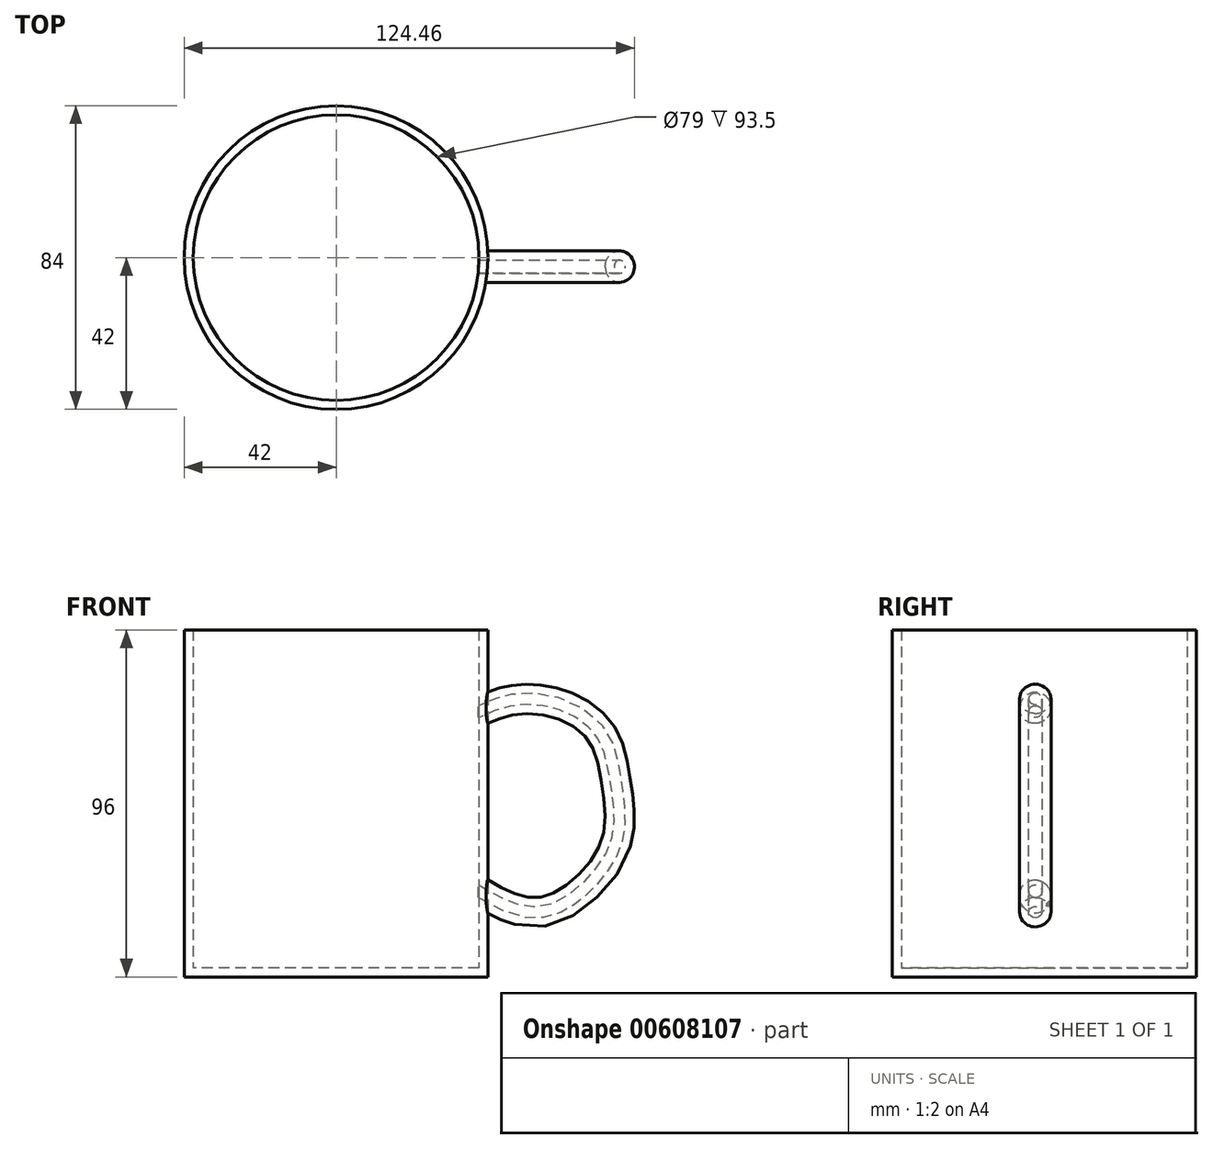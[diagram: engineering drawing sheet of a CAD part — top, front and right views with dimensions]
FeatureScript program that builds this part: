
annotation { "Feature Type Name" : "Feature", "Feature Type Description" : "" }
export const myFeature = defineFeature(function(context is Context, id is Id, definition is map)
    precondition{}
    {
        {
            var Q0;
            Q0=qCreatedBy(makeId("Top.planeOp"),FACE);
            var sketch = newSketch(context, id + "F0", { "sketchPlane" : qUnion([Q0])});
            skCircle(sketch, "E0", {"center": v(0, 0) * mm, "radius": 42 * mm});
            skSolve(sketch);
        }
        {
            var Q0;
            Q0 = qSketchRegion(id + "F0", true);
            extrude(context, id + "F1", {"entities" : qUnion([Q0]), "depth" : 96 * mm, "offsetDistance" : 25 * mm});
        }
        {
            var Q0;
            Q0=qCreatedBy(makeId("Front.planeOp"),FACE);
            var sketch = newSketch(context, id + "F2", { "sketchPlane" : qUnion([Q0])});
            skFitSpline(sketch, "E1", {"points": [v(40.8, 71.96) * mm, v(48.66, 74.63) * mm, v(60.67, 73.85) * mm, v(71.49, 66.59) * mm, v(75.33, 54.8) * mm, v(76.11, 39.69) * mm, v(69.57, 27.89) * mm, v(58.72, 20.43) * mm, v(49.27, 20.86) * mm, v(39.83, 25.62) * mm], "startDerivative": vector(79.14, 34.52) * mm, "endDerivative": vector(-88.75, 52.54) * mm});
            skSolve(sketch);
        }
        {
            var Q0;
            Q0=qCreatedBy(makeId("Right.planeOp"),FACE);
            cPlane(context, id + "F3", {"entities" : qUnion([Q0]), "cplaneType" : CPlaneType.OFFSET, "offset" : 42 * mm, "width" : 150 * mm, "height" : 150 * mm});
        }
        {
            var Q0;
            Q0=qCreatedBy(id+"F3.planeOp",FACE);
            var sketch = newSketch(context, id + "F4", { "sketchPlane" : qUnion([Q0])});
            skCircle(sketch, "E2", {"center": v(-2.5, 74.52) * mm, "radius": 4.35 * mm});
            skSolve(sketch);
        }
        {
            var Q0;
            Q0=makeQuery(id+"F4.imprint","IMPRINT",FACE,{"disambiguationData":[TD([[makeQuery(id+"F4.imprint","IMPRINT",EDGE,{"derivedFrom":sQuery(id+"F4.wireOp",EDGE,"E2")}),1.0]])]});
            var Q1;
            Q1=sQuery(id+"F2.wireOp",EDGE,"E1");
            sweep(context, id + "F5", {"operationType" : NewBodyOperationType.ADD, "profiles" : qUnion([Q0]), "path" : qUnion([Q1])});
        }
        {
            var Q0;
            Q0=makeQuery(id+"F1.opExtrude","CAP_FACE",FACE,{"disambiguationData":[OSD([sQuery(id+"F0.wireOp",EDGE,"E0")])],"isStart":false});
            shell(context, id + "F6", {"entities" : qUnion([Q0]), "thickness" : 2.5 * mm});
        }
    });
